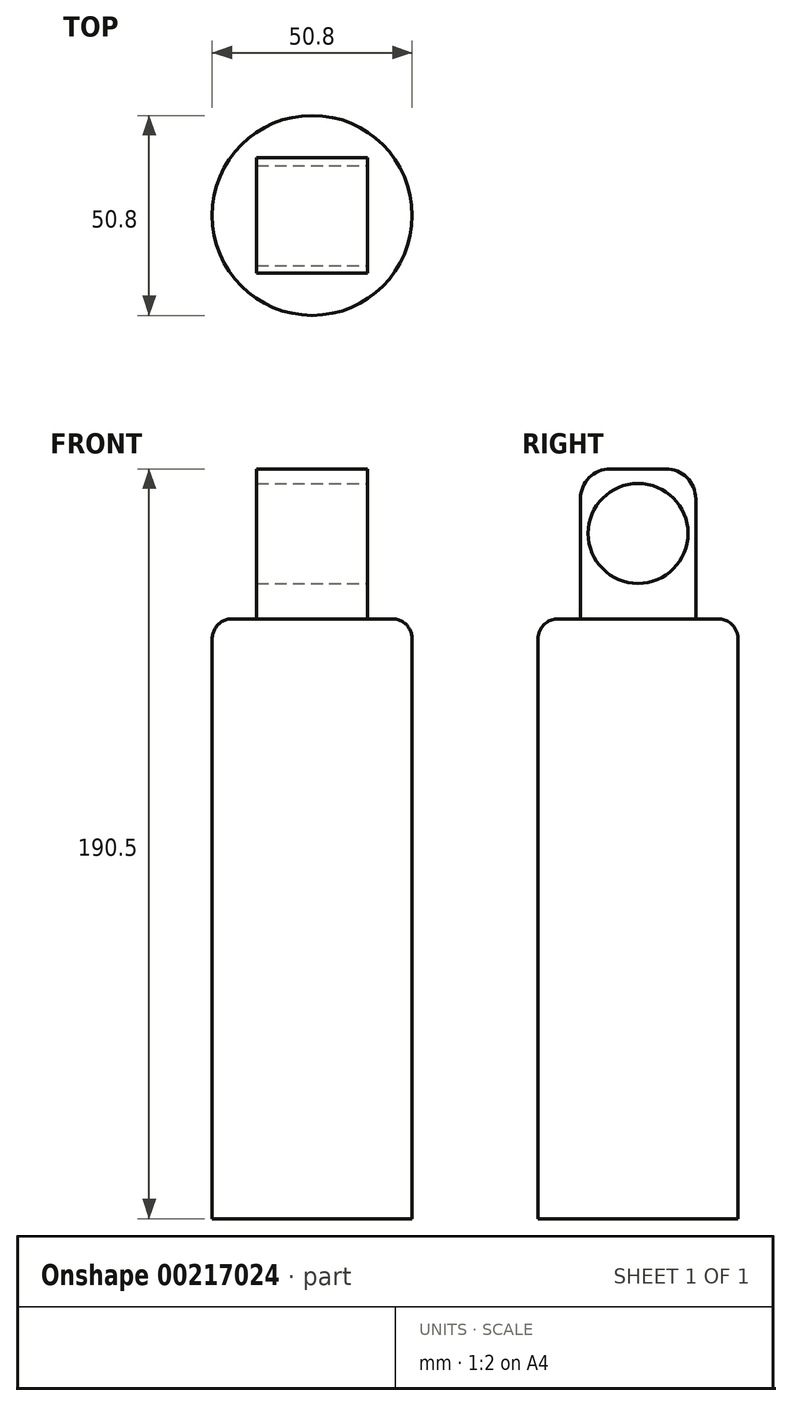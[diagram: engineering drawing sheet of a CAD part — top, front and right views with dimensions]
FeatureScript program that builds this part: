
annotation { "Feature Type Name" : "Feature", "Feature Type Description" : "" }
export const myFeature = defineFeature(function(context is Context, id is Id, definition is map)
    precondition{}
    {
        {
            var Q0;
            Q0=qCreatedBy(makeId("Top.planeOp"),FACE);
            var sketch = newSketch(context, id + "F0", { "sketchPlane" : qUnion([Q0])});
            skCircle(sketch, "E0", {"center": v(0, 0) * mm, "radius": 25.4 * mm});
            skSolve(sketch);
        }
        {
            var Q0;
            Q0 = qSketchRegion(id + "F0", true);
            extrude(context, id + "F1", {"entities" : qUnion([Q0]), "depth" : 152.4 * mm});
        }
        {
            var Q0;
            Q0=makeQuery(id+"F1.opExtrude","CAP_EDGE",EDGE,{"disambiguationData":[OSD([sQuery(id+"F0.wireOp",EDGE,"E0")])],"isStart":false});
            fillet(context, id + "F2", {"entities" : qUnion([Q0]), "radius" : 5.08 * mm, "tangentPropagation" : true, "allowEdgeOverflow" : false});
        }
        {
            var Q0;
            Q0=makeQuery(id+"F1.opExtrude","CAP_FACE",FACE,{"disambiguationData":[OSD([sQuery(id+"F0.wireOp",EDGE,"E0")])],"isStart":false});
            var sketch = newSketch(context, id + "F3", { "sketchPlane" : qUnion([Q0])});
            skLineSegment(sketch, "E1.bottom", {"start": v(14.08, -14.65) * mm, "end": v(-14.08, -14.65) * mm});
            skLineSegment(sketch, "E1.top", {"start": v(14.08, 14.65) * mm, "end": v(-14.08, 14.65) * mm});
            skLineSegment(sketch, "E1.left", {"start": v(14.08, -14.65) * mm, "end": v(14.08, 14.65) * mm});
            skLineSegment(sketch, "E1.right", {"start": v(-14.08, -14.65) * mm, "end": v(-14.08, 14.65) * mm});
            skPoint(sketch, "E1.middle", {"position": v(0, 0) * mm});
            skSolve(sketch);
        }
        {
            var Q0;
            Q0=makeQuery(id+"F3.imprint","IMPRINT",FACE,{"disambiguationData":[TD([[makeQuery(id+"F3.imprint","IMPRINT",EDGE,{"derivedFrom":sQuery(id+"F3.wireOp",EDGE,"E1.bottom")}),-1.0]])]});
            extrude(context, id + "F4", {"entities" : qUnion([Q0]), "operationType" : NewBodyOperationType.ADD, "depth" : 38.1 * mm});
        }
        {
            var Q0;
            Q0=makeQuery(id+"F4.opExtrude","SWEPT_FACE",FACE,{"disambiguationData":[OSD([sQuery(id+"F3.wireOp",EDGE,"E1.left")])]});
            var sketch = newSketch(context, id + "F5", { "sketchPlane" : qUnion([Q0])});
            skCircle(sketch, "E2", {"center": v(0, 174.1) * mm, "radius": 12.7 * mm});
            skSolve(sketch);
        }
        {
            var Q0;
            Q0=makeQuery(id+"F4.opExtrude","CAP_EDGE",EDGE,{"disambiguationData":[OSD([sQuery(id+"F3.wireOp",EDGE,"E1.bottom")])],"isStart":false});
            var Q1;
            Q1=makeQuery(id+"F4.opExtrude","CAP_EDGE",EDGE,{"disambiguationData":[OSD([sQuery(id+"F3.wireOp",EDGE,"E1.top")])],"isStart":false});
            fillet(context, id + "F6", {"entities" : qUnion([Q0, Q1]), "radius" : 7.62 * mm, "tangentPropagation" : true, "allowEdgeOverflow" : false});
        }
        {
            var Q0;
            Q0=makeQuery(id+"F5.imprint","IMPRINT",FACE,{"disambiguationData":[TD([[makeQuery(id+"F5.imprint","IMPRINT",EDGE,{"derivedFrom":sQuery(id+"F5.wireOp",EDGE,"E2")}),1.0]])]});
            extrude(context, id + "F7", {"entities" : qUnion([Q0]), "operationType" : NewBodyOperationType.REMOVE, "endBound" : BoundingType.THROUGH_ALL, "oppositeDirection" : true, "depth" : 25.4 * mm});
        }
    });
